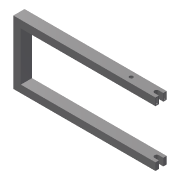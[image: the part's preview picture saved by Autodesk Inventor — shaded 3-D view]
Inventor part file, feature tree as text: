
AUTODESK INVENTOR PART (.ipt)
format: ipt  version: 2015 (Build 190159000, 159)  size: 153,600 bytes
history: native  units: mm
features: shell x2, sweep x1, extrude x1, hole x1, sketch x1
ambient origin geometry x8: Origin, YZ Plane, XZ Plane, XY Plane, X Axis, Y Axis, Z Axis, Center Point
bodies: Solid1 (feature_tree)
feature tree (6):
  sweep  "Sweep1"
  extrude  "Extrusion1"  Depth=20.0mm
  shell  "Shell1"  Thickness=0.0mm
  shell  "Shell2"  Thickness=12.0mm
  hole  "Hole1"  [1 undecoded]
  sketch  "Sketch1"  dims[d7=370.0mm d8=150.0mm d9=370.0mm d12=0.0mm d13=0.0mm d14=12.0mm d15=12.0mm d16=10.0mm d17=0.0mm d20=15.0mm d21=10.0mm d22=30.0mm d23=20.0mm d24=30.0mm d25=3.0mm d26=2.5mm d27=2.5mm d28=15.0mm d29=80.0mm d30=10.0mm d31=6.0mm d32=4.0mm d33=2.0mm d34=90.0deg d35=20.0mm d36=20.594885mm]
note: 1 required parameter value undecoded (feature->parameter linkage not recoverable at this tier; creation-order binding heuristic only, values carry confidence <= 0.55)
